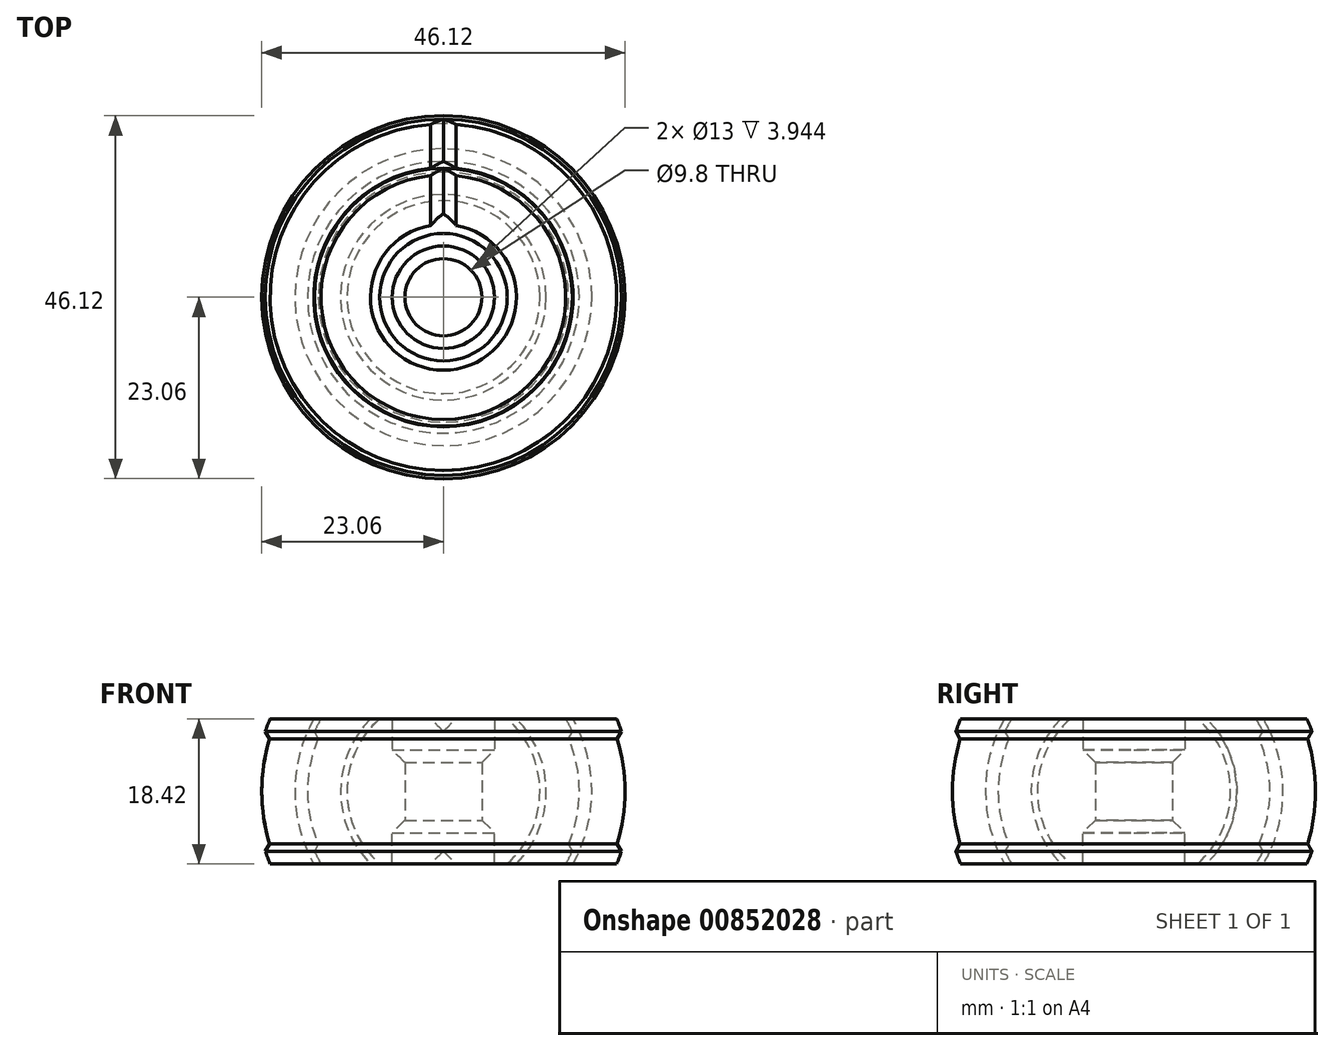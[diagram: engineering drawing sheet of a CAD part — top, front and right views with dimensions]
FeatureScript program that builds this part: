
annotation { "Feature Type Name" : "Feature", "Feature Type Description" : "" }
export const myFeature = defineFeature(function(context is Context, id is Id, definition is map)
    precondition{}
    {
        {
            assignVariable(context, id + "F0", {"name" : "Extrusion", "anyValue" : 0.4});
        }
        {
            assignVariable(context, id + "F1", {"name" : "Shells", "anyValue" : 2});
        }
        {
            assignVariable(context, id + "F2", {"name" : "MinStruct", "anyValue" : getVariable(context, 'Extrusion') * getVariable(context, 'Shells')});
        }
        {
            assignVariable(context, id + "F3", {"name" : "Wall", "anyValue" : getVariable(context, 'MinStruct') * 2});
        }
        {
            var Q0;
            Q0=qCreatedBy(makeId("Front.planeOp"),FACE);
            var sketch = newSketch(context, id + "F4", { "sketchPlane" : qUnion([Q0])});
            skCircle(sketch, "E0", {"center": v(0, 9.2) * mm, "radius": 6.5 * mm, "construction": true});
            skLineSegment(sketch, "E1", {"start": v(0, 9.2) * mm, "end": v(6.5, 9.2) * mm, "construction": true});
            skCircle(sketch, "E2", {"center": v(0, 0) * mm, "radius": 12.26 * mm});
            skCircle(sketch, "E3", {"center": v(0, 0) * mm, "radius": 13.06 * mm});
            skCircle(sketch, "E4", {"center": v(0, 0) * mm, "radius": 18.06 * mm});
            skCircle(sketch, "E5", {"center": v(0, 0) * mm, "radius": 18.86 * mm});
            skCircle(sketch, "E6", {"center": v(0, 0) * mm, "radius": 23.86 * mm});
            skLineSegment(sketch, "E7", {"start": v(0, 9.2) * mm, "end": v(22.02, 9.2) * mm});
            skPoint(sketch, "E8", {"position": v(16.46, 9.2) * mm});
            skPoint(sketch, "E9", {"position": v(18.06, 0) * mm});
            skLineSegment(sketch, "E10", {"start": v(0, 0) * mm, "end": v(12.26, 0) * mm, "construction": true});
            skLineSegment(sketch, "E11", {"start": v(13.06, 0) * mm, "end": v(18.06, 0) * mm, "construction": true});
            skLineSegment(sketch, "E12", {"start": v(18.86, 0) * mm, "end": v(23.86, 0) * mm, "construction": true});
            skLineSegment(sketch, "E13", {"start": v(6.5, 9.2) * mm, "end": v(6.5, 9.2) * mm});
            skPoint(sketch, "E14", {"position": v(8.1, 9.2) * mm});
            skLineSegment(sketch, "E15", {"start": v(6.5, 9.2) * mm, "end": v(6.5, 5.26) * mm});
            skLineSegment(sketch, "E16", {"start": v(6.5, 5.26) * mm, "end": v(4.9, 3.66) * mm});
            skLineSegment(sketch, "E17", {"start": v(4.9, 3.66) * mm, "end": v(4.9, 0) * mm});
            skPoint(sketch, "E18", {"position": v(0, 12.26) * mm});
            skLineSegment(sketch, "E19", {"start": v(0, 0) * mm, "end": v(0, 9.2) * mm});
            skLineSegment(sketch, "E20", {"start": v(0, 0) * mm, "end": v(23.86, 0) * mm});
            skLineSegment(sketch, "E21", {"start": v(16.38, 7.6) * mm, "end": v(11.85, 5.5) * mm, "construction": true});
            skLineSegment(sketch, "E22", {"start": v(22.62, 7.6) * mm, "end": v(17.88, 6.01) * mm, "construction": true});
            skLineSegment(sketch, "E23", {"start": v(16.38, 7.6) * mm, "end": v(15.89, 6.75) * mm});
            skLineSegment(sketch, "E24", {"start": v(22.62, 7.6) * mm, "end": v(22.08, 6.67) * mm});
            skArc(sketch, "E25", {"start": v(17.26, 0) * mm, "mid": v(16.92, 3.44) * mm, "end": v(15.89, 6.75) * mm});
            skArc(sketch, "E26", {"start": v(23.06, 0) * mm, "mid": v(22.82, 3.37) * mm, "end": v(22.08, 6.67) * mm});
            skSolve(sketch);
        }
        {
            var Q0;
            {var subQ0=sQuery(id+"F4.wireOp",EDGE,"E15");Q0=makeQuery(id+"F4.imprint","IMPRINT",FACE,{"disambiguationData":[TD([[makeQuery(id+"F4.imprint","IMPRINT",EDGE,{"derivedFrom":subQ0}),1.0]])]});}
            var Q1;
            {var subQ0=sQuery(id+"F4.wireOp",EDGE,"E7");var subQ1=sQuery(id+"F4.wireOp",EDGE,"E3");var subQ2=makeQuery(id+"F4.imprint","INTERSECT",VERTEX,{"derivedFrom":[subQ1,subQ0]});Q1=makeQuery(id+"F4.imprint","IMPRINT",FACE,{"disambiguationData":[TD([[makeQuery(id+"F4.imprint","IMPRINT",EDGE,{"disambiguationData":[TD([[subQ2,1.0]])],"derivedFrom":subQ1}),-1.0]])]});}
            var Q2;
            {var subQ0=sQuery(id+"F4.wireOp",EDGE,"E7");var subQ1=sQuery(id+"F4.wireOp",EDGE,"E5");var subQ2=makeQuery(id+"F4.imprint","INTERSECT",VERTEX,{"derivedFrom":[subQ1,subQ0]});Q2=makeQuery(id+"F4.imprint","IMPRINT",FACE,{"disambiguationData":[TD([[makeQuery(id+"F4.imprint","IMPRINT",EDGE,{"disambiguationData":[TD([[subQ2,1.0]])],"derivedFrom":subQ1}),-1.0]])]});}
            var Q3;
            Q3=sQuery(id+"F4.wireOp",EDGE,"E19");
            revolve(context, id + "F5", {"surfaceOperationType" : NewSurfaceOperationType.NEW, "entities" : qUnion([Q0, Q1, Q2]), "axis" : qUnion([Q3]), "revolveType" : RevolveType.SYMMETRIC, "angle" : 180 * degree});
        }
        {
            var Q0;
            {var subQ0=sQuery(id+"F4.wireOp",EDGE,"E7");Q0=makeQuery(id+"F5.opRevolve","CAP_EDGE",EDGE,{"disambiguationData":[OSD([subQ0]),TDD([makeQuery(id+"F4.imprint","IMPRINT",EDGE,{"disambiguationData":[TD([[makeQuery(id+"F4.imprint","INTERSECT",VERTEX,{"derivedFrom":[sQuery(id+"F4.wireOp",EDGE,"E6"),subQ0]}),1.0]])],"derivedFrom":subQ0})])],"isStart":false});}
            var Q1;
            {var subQ0=sQuery(id+"F4.wireOp",EDGE,"E7");Q1=makeQuery(id+"F5.opRevolve","CAP_EDGE",EDGE,{"disambiguationData":[OSD([subQ0]),TDD([makeQuery(id+"F4.imprint","IMPRINT",EDGE,{"disambiguationData":[TD([[makeQuery(id+"F4.imprint","INTERSECT",VERTEX,{"derivedFrom":[sQuery(id+"F4.wireOp",EDGE,"E3"),subQ0]}),-1.0]])],"derivedFrom":subQ0})])],"isStart":false});}
            chamfer(context, id + "F6", {"entities" : qUnion([Q0, Q1]), "width" : (getVariable(context, 'Wall')) * mm, "tangentPropagation" : true});
        }
        {
            var Q0;
            Q0=makeQuery(id+"F5.opRevolve","SWEPT_BODY",BODY,{"disambiguationData":[OSD([sQuery(id+"F4.wireOp",EDGE,"E5"),sQuery(id+"F4.wireOp",EDGE,"E6"),sQuery(id+"F4.wireOp",EDGE,"E7"),sQuery(id+"F4.wireOp",EDGE,"E20"),sQuery(id+"F4.wireOp",EDGE,"E24"),sQuery(id+"F4.wireOp",EDGE,"E26")])]});
            var Q1;
            Q1=makeQuery(id+"F5.opRevolve","SWEPT_BODY",BODY,{"disambiguationData":[OSD([sQuery(id+"F4.wireOp",EDGE,"E3"),sQuery(id+"F4.wireOp",EDGE,"E4"),sQuery(id+"F4.wireOp",EDGE,"E7"),sQuery(id+"F4.wireOp",EDGE,"E20"),sQuery(id+"F4.wireOp",EDGE,"E23"),sQuery(id+"F4.wireOp",EDGE,"E25")])]});
            var Q2;
            Q2=makeQuery(id+"F5.opRevolve","SWEPT_BODY",BODY,{"disambiguationData":[OSD([sQuery(id+"F4.wireOp",EDGE,"E2"),sQuery(id+"F4.wireOp",EDGE,"E7"),sQuery(id+"F4.wireOp",EDGE,"E15"),sQuery(id+"F4.wireOp",EDGE,"E16"),sQuery(id+"F4.wireOp",EDGE,"E17"),sQuery(id+"F4.wireOp",EDGE,"E20")])]});
            var Q3;
            {var subQ0=sQuery(id+"F4.wireOp",EDGE,"E20");Q3=makeQuery(id+"F5.opRevolve","SWEPT_FACE",FACE,{"disambiguationData":[OSD([subQ0]),TDD([makeQuery(id+"F4.imprint","IMPRINT",EDGE,{"disambiguationData":[TD([[makeQuery(id+"F4.imprint","INTERSECT",VERTEX,{"derivedFrom":[subQ0,sQuery(id+"F4.wireOp",EDGE,"E26")]}),1.0]])],"derivedFrom":subQ0})])]});}
            mirror(context, id + "F7", {"operationType" : NewBodyOperationType.ADD, "entities" : qUnion([Q0, Q1, Q2]), "mirrorPlane" : qUnion([Q3])});
        }
        {
            var Q0;
            Q0=makeQuery(id+"F5.opRevolve","SWEPT_BODY",BODY,{"disambiguationData":[OSD([sQuery(id+"F4.wireOp",EDGE,"E5"),sQuery(id+"F4.wireOp",EDGE,"E6"),sQuery(id+"F4.wireOp",EDGE,"E7"),sQuery(id+"F4.wireOp",EDGE,"E20"),sQuery(id+"F4.wireOp",EDGE,"E24"),sQuery(id+"F4.wireOp",EDGE,"E26")])]});
            var Q1;
            Q1=makeQuery(id+"F5.opRevolve","SWEPT_BODY",BODY,{"disambiguationData":[OSD([sQuery(id+"F4.wireOp",EDGE,"E3"),sQuery(id+"F4.wireOp",EDGE,"E4"),sQuery(id+"F4.wireOp",EDGE,"E7"),sQuery(id+"F4.wireOp",EDGE,"E20"),sQuery(id+"F4.wireOp",EDGE,"E23"),sQuery(id+"F4.wireOp",EDGE,"E25")])]});
            var Q2;
            Q2=makeQuery(id+"F5.opRevolve","SWEPT_BODY",BODY,{"disambiguationData":[OSD([sQuery(id+"F4.wireOp",EDGE,"E2"),sQuery(id+"F4.wireOp",EDGE,"E7"),sQuery(id+"F4.wireOp",EDGE,"E15"),sQuery(id+"F4.wireOp",EDGE,"E16"),sQuery(id+"F4.wireOp",EDGE,"E17"),sQuery(id+"F4.wireOp",EDGE,"E20")])]});
            var Q3;
            {var subQ0=makeQuery(id+"F5.opRevolve","CAP_FACE",FACE,{"disambiguationData":[OSD([sQuery(id+"F4.wireOp",EDGE,"E2"),sQuery(id+"F4.wireOp",EDGE,"E7"),sQuery(id+"F4.wireOp",EDGE,"E15"),sQuery(id+"F4.wireOp",EDGE,"E16"),sQuery(id+"F4.wireOp",EDGE,"E17"),sQuery(id+"F4.wireOp",EDGE,"E20")])],"isStart":false});Q3=makeQuery(id+"F7.boolean.opBoolean","MERGE",FACE,{"derivedFrom":[subQ0,makeQuery(id+"F7.opPattern","COPY",FACE,{"derivedFrom":subQ0,"instanceName":"1"})]});}
            mirror(context, id + "F8", {"operationType" : NewBodyOperationType.ADD, "entities" : qUnion([Q0, Q1, Q2]), "mirrorPlane" : qUnion([Q3])});
        }
    });
